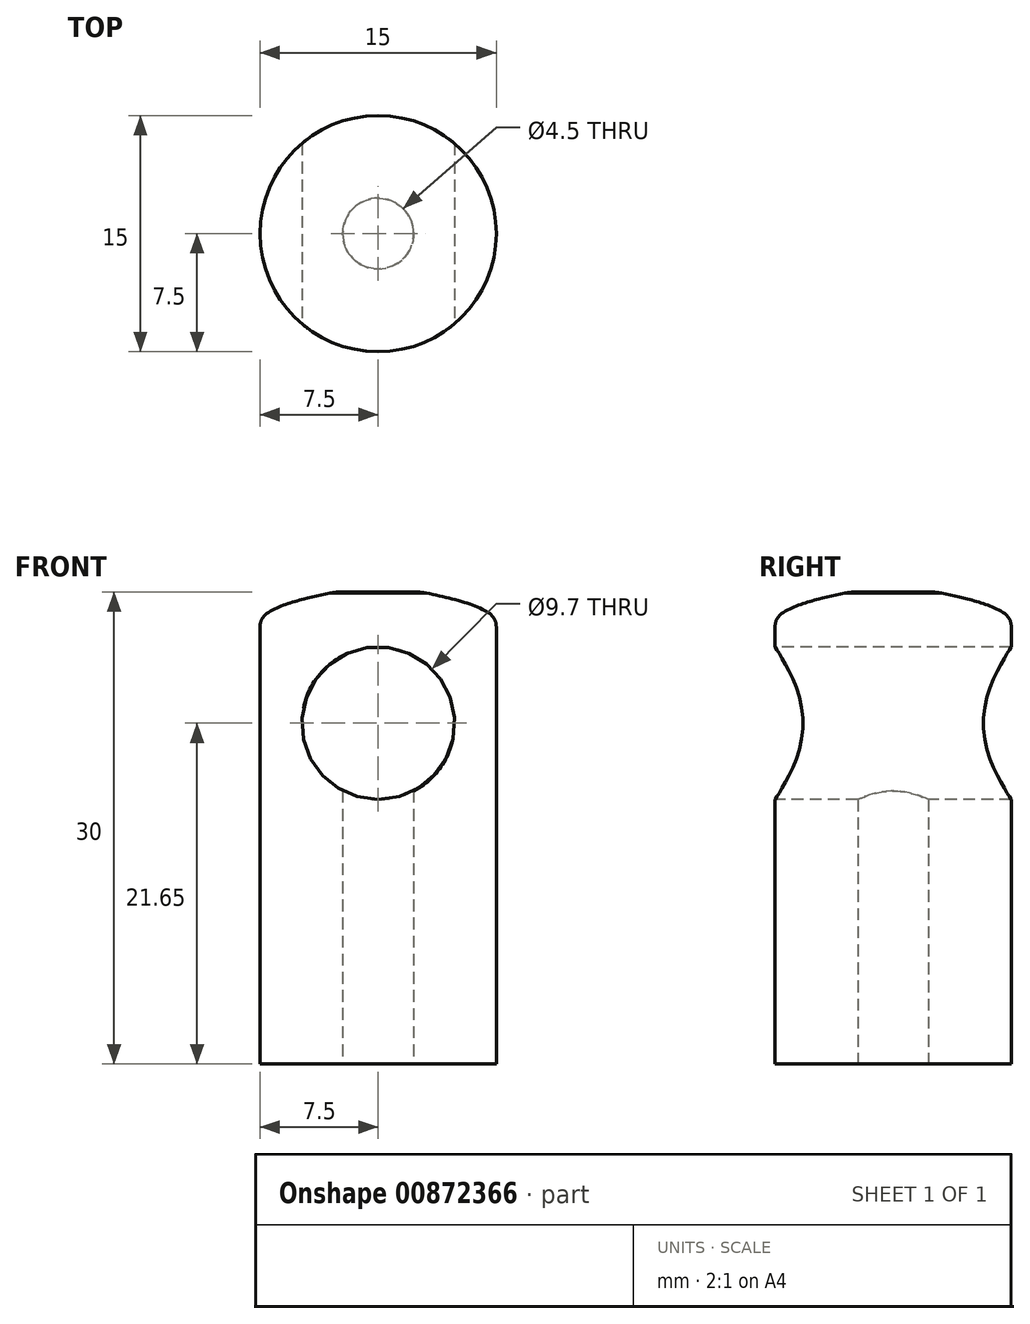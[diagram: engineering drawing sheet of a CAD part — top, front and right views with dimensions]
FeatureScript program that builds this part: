
annotation { "Feature Type Name" : "Feature", "Feature Type Description" : "" }
export const myFeature = defineFeature(function(context is Context, id is Id, definition is map)
    precondition{}
    {
        {
            var Q0;
            Q0=qCreatedBy(makeId("Top.planeOp"),FACE);
            var sketch = newSketch(context, id + "F0", { "sketchPlane" : qUnion([Q0])});
            skCircle(sketch, "E0", {"center": v(0, 0) * mm, "radius": 7.5 * mm});
            skSolve(sketch);
        }
        {
            var Q0;
            Q0=makeQuery(id+"F0.imprint","IMPRINT",FACE,{"disambiguationData":[TD([[makeQuery(id+"F0.imprint","IMPRINT",EDGE,{"derivedFrom":sQuery(id+"F0.wireOp",EDGE,"E0")}),1.0]])]});
            extrude(context, id + "F1", {"entities" : qUnion([Q0]), "depth" : 30 * mm, "offsetDistance" : 25 * mm});
        }
        {
            var Q0;
            Q0=qCreatedBy(makeId("Front.planeOp"),FACE);
            var sketch = newSketch(context, id + "F2", { "sketchPlane" : qUnion([Q0])});
            skCircle(sketch, "E1", {"center": v(0, 21.65) * mm, "radius": 4.85 * mm});
            skSolve(sketch);
        }
        {
            var Q0;
            Q0 = qSketchRegion(id + "F2", true);
            extrude(context, id + "F3", {"entities" : qUnion([Q0]), "operationType" : NewBodyOperationType.REMOVE, "endBound" : BoundingType.THROUGH_ALL, "oppositeDirection" : true, "depth" : 25 * mm, "offsetDistance" : 25 * mm, "hasSecondDirection" : true, "secondDirectionOppositeDirection" : false, "secondDirectionDepth" : 25 * mm});
        }
        {
            var Q0;
            Q0=makeQuery(id+"F1.opExtrude","CAP_FACE",FACE,{"disambiguationData":[OSD([sQuery(id+"F0.wireOp",EDGE,"E0")])],"isStart":true});
            var sketch = newSketch(context, id + "F4", { "sketchPlane" : qUnion([Q0])});
            skCircle(sketch, "E2", {"center": v(0, 0) * mm, "radius": 2.25 * mm});
            skSolve(sketch);
        }
        {
            var Q0;
            Q0 = qSketchRegion(id + "F4", true);
            extrude(context, id + "F5", {"entities" : qUnion([Q0]), "operationType" : NewBodyOperationType.REMOVE, "oppositeDirection" : true, "depth" : 20 * mm, "offsetDistance" : 25 * mm});
        }
        {
            var Q0;
            Q0=qCreatedBy(makeId("Front.planeOp"),FACE);
            var sketch = newSketch(context, id + "F6", { "sketchPlane" : qUnion([Q0])});
            skFitSpline(sketch, "E3", {"points": [v(-7.5, 28) * mm, v(0, 30.3) * mm], "startDerivative": vector(0.03, 4.1) * mm, "endDerivative": vector(3.61, -0.04) * mm});
            skLineSegment(sketch, "E4", {"start": v(-7.5, 28) * mm, "end": v(-7.5, 30.3) * mm});
            skLineSegment(sketch, "E5", {"start": v(-7.5, 30.3) * mm, "end": v(0, 30.3) * mm});
            skLineSegment(sketch, "E6", {"start": v(0, 31.18) * mm, "end": v(0, 25.84) * mm, "construction": true});
            skSolve(sketch);
        }
        {
            var Q0;
            Q0=makeQuery(id+"F6.imprint","IMPRINT",FACE,{"disambiguationData":[TD([[makeQuery(id+"F6.imprint","IMPRINT",EDGE,{"derivedFrom":sQuery(id+"F6.wireOp",EDGE,"E3")}),1.0]])]});
            var Q1;
            Q1=sQuery(id+"F6.wireOp",EDGE,"E6");
            revolve(context, id + "F7", {"operationType" : NewBodyOperationType.REMOVE, "surfaceOperationType" : NewSurfaceOperationType.NEW, "entities" : qUnion([Q0]), "axis" : qUnion([Q1]), "revolveType" : RevolveType.FULL});
        }
        {
            var Q0;
            Q0=makeQuery(id+"F7.boolean.opBoolean","INTERSECT",EDGE,{"derivedFrom":[makeQuery(id+"F1.opExtrude","CAP_FACE",FACE,{"disambiguationData":[OSD([sQuery(id+"F0.wireOp",EDGE,"E0")])],"isStart":false}),makeQuery(id+"F7.opRevolve","SWEPT_FACE",FACE,{"disambiguationData":[OSD([sQuery(id+"F6.wireOp",EDGE,"E3")])]})]});
            fillet(context, id + "F8", {"entities" : qUnion([Q0]), "radius" : 5 * mm, "tangentPropagation" : true, "allowEdgeOverflow" : false});
        }
        {
            var Q0;
            Q0=makeQuery(id+"F7.boolean.opBoolean","INTERSECT",EDGE,{"derivedFrom":[makeQuery(id+"F1.opExtrude","SWEPT_FACE",FACE,{"disambiguationData":[OSD([sQuery(id+"F0.wireOp",EDGE,"E0")])]}),makeQuery(id+"F7.opRevolve","SWEPT_FACE",FACE,{"disambiguationData":[OSD([sQuery(id+"F6.wireOp",EDGE,"E3")])]})]});
            fillet(context, id + "F9", {"entities" : qUnion([Q0]), "radius" : 1 * mm, "tangentPropagation" : true, "allowEdgeOverflow" : false});
        }
    });
